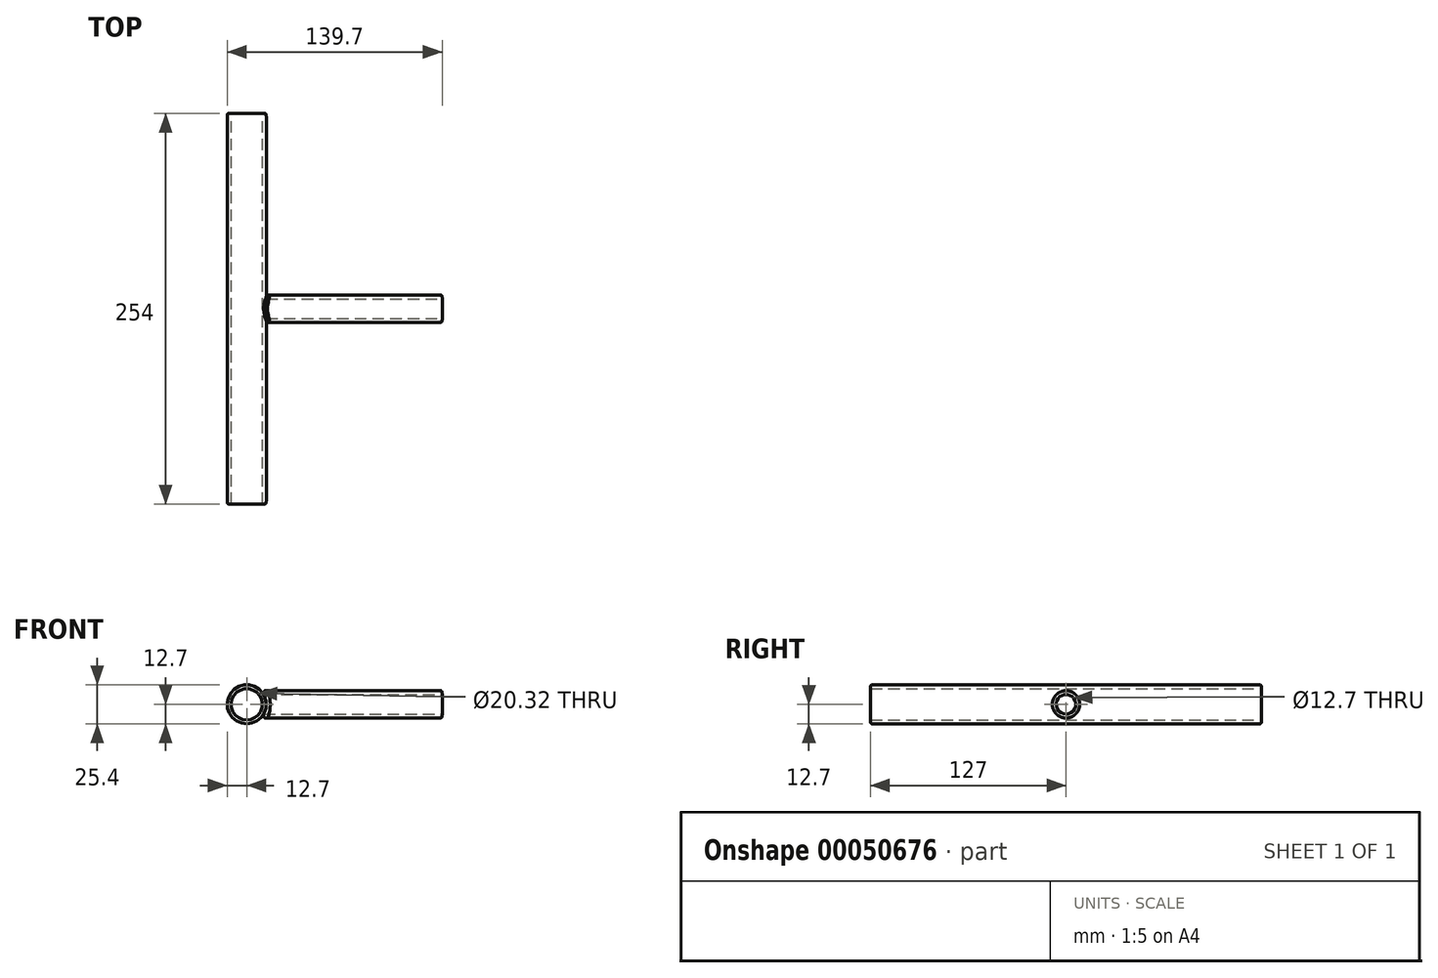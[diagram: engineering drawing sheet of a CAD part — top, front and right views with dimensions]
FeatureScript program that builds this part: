
annotation { "Feature Type Name" : "Feature", "Feature Type Description" : "" }
export const myFeature = defineFeature(function(context is Context, id is Id, definition is map)
    precondition{}
    {
        {
            var Q0;
            Q0=qCreatedBy(makeId("Front.planeOp"),FACE);
            var sketch = newSketch(context, id + "F0", { "sketchPlane" : qUnion([Q0])});
            skCircle(sketch, "E0", {"center": v(0, 0) * mm, "radius": 10.16 * mm});
            skCircle(sketch, "E1", {"center": v(0, 0) * mm, "radius": 12.7 * mm});
            skSolve(sketch);
        }
        {
            var Q0;
            Q0 = qSketchRegion(id + "F0", true);
            extrude(context, id + "F1", {"entities" : qUnion([Q0]), "depth" : 254 * mm});
        }
        {
            var Q0;
            Q0=qCreatedBy(makeId("Right.planeOp"),FACE);
            cPlane(context, id + "F2", {"entities" : qUnion([Q0]), "cplaneType" : CPlaneType.OFFSET, "offset" : 127 * mm, "width" : 152.4 * mm, "height" : 152.4 * mm});
        }
        {
            var Q0;
            Q0=qCreatedBy(id+"F2.planeOp",FACE);
            var sketch = newSketch(context, id + "F3", { "sketchPlane" : qUnion([Q0])});
            skCircle(sketch, "E2", {"center": v(-127, 0) * mm, "radius": 6.35 * mm});
            skCircle(sketch, "E3", {"center": v(-127, 0) * mm, "radius": 8.9 * mm});
            skSolve(sketch);
        }
        {
            var Q0;
            Q0 = qSketchRegion(id + "F3", true);
            extrude(context, id + "F4", {"entities" : qUnion([Q0]), "endBound" : BoundingType.UP_TO_NEXT, "oppositeDirection" : true, "depth" : 25.4 * mm});
        }
        {
            var Q0;
            Q0=makeQuery(id+"F1.opExtrude","SWEPT_FACE",FACE,{"disambiguationData":[OSD([sQuery(id+"F0.wireOp",EDGE,"E1")])]});
            var Q1;
            Q1=makeQuery(id+"F4.opExtrude","SWEPT_FACE",FACE,{"disambiguationData":[OSD([sQuery(id+"F3.wireOp",EDGE,"E3")])]});
            fillet(context, id + "F5", {"entities" : qUnion([Q0, Q1]), "radius" : 2.54 * mm, "rho" : 0.75, "crossSection" : FilletCrossSection.CONIC, "allowEdgeOverflow" : false});
        }
    });
